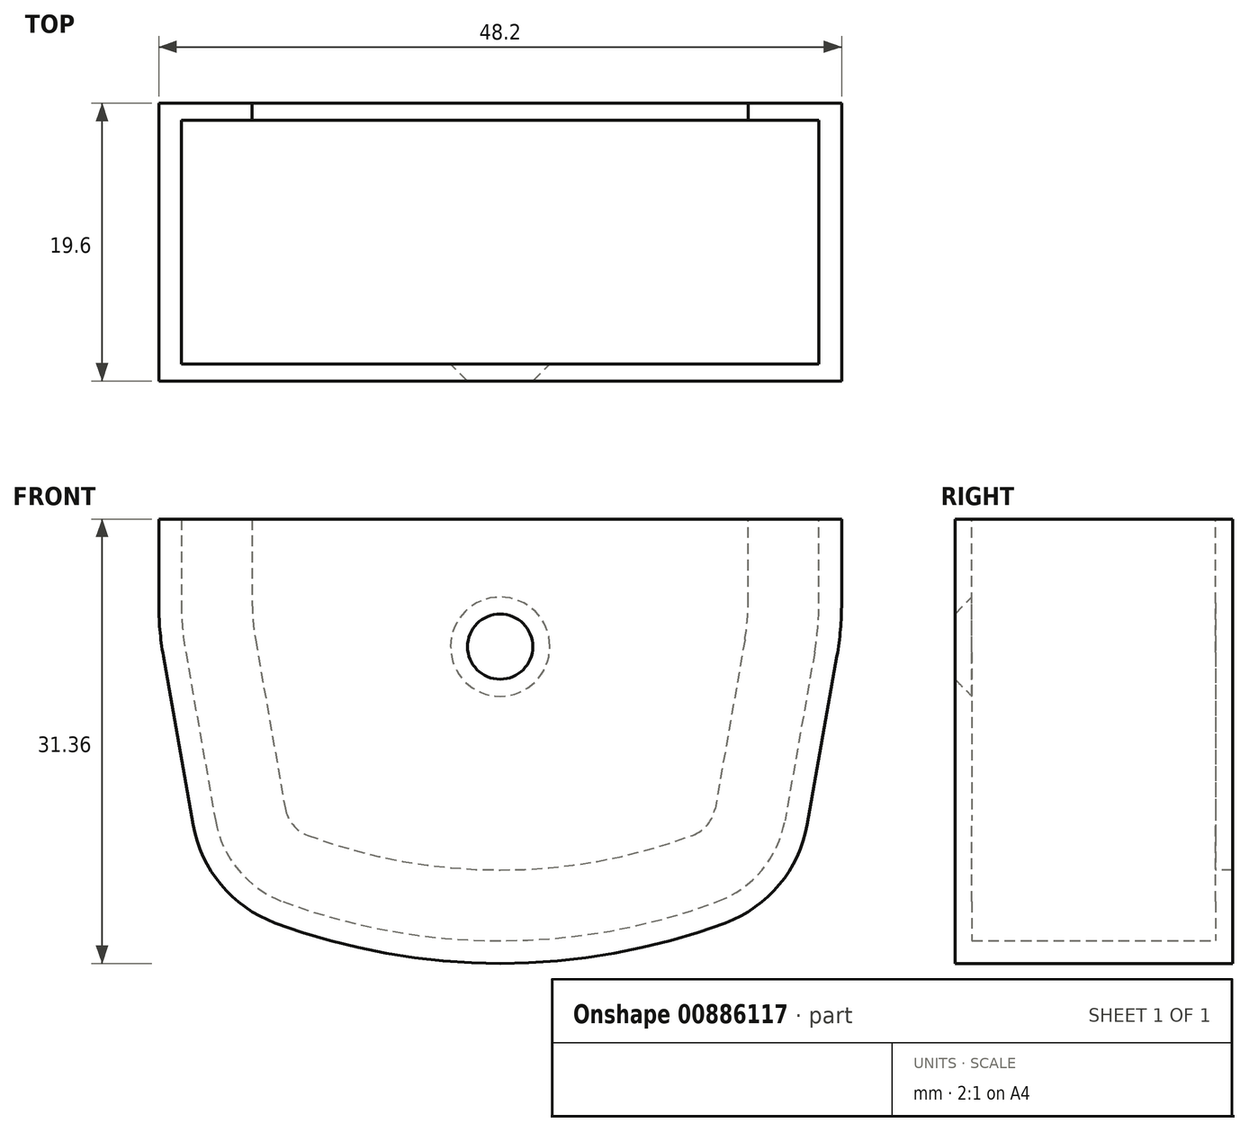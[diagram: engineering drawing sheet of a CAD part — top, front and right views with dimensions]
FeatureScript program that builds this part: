
annotation { "Feature Type Name" : "Feature", "Feature Type Description" : "" }
export const myFeature = defineFeature(function(context is Context, id is Id, definition is map)
    precondition{}
    {
        {
            var Q0;
            Q0=qCreatedBy(makeId("Front.planeOp"),FACE);
            var sketch = newSketch(context, id + "F0", { "sketchPlane" : qUnion([Q0])});
            skLineSegment(sketch, "E0", {"start": v(-22.2, 17.61) * mm, "end": v(-20.1, 5.73) * mm});
            skArc(sketch, "E1.filletArc", {"start": v(-20.1, 5.73) * mm, "mid": v(-18.48, 2.23) * mm, "end": v(-15.33, 0) * mm});
            skArc(sketch, "E2.MirrorCS", {"start": v(20.1, 5.73) * mm, "mid": v(18.48, 2.23) * mm, "end": v(15.33, 0) * mm});
            skLineSegment(sketch, "E3.MirrorCS", {"start": v(22.2, 17.61) * mm, "end": v(20.1, 5.73) * mm});
            skArc(sketch, "E4", {"start": v(-15.33, 0) * mm, "mid": v(0, -2.76) * mm, "end": v(15.33, 0) * mm});
            skLineSegment(sketch, "E5", {"start": v(-22.5, 27) * mm, "end": v(-22.5, 21.09) * mm});
            skLineSegment(sketch, "E6", {"start": v(22.5, 21.09) * mm, "end": v(22.5, 27) * mm});
            skPoint(sketch, "E7.visualSharp", {"position": v(-22.5, 19.34) * mm});
            skArc(sketch, "E7.filletArc", {"start": v(-22.5, 21.09) * mm, "mid": v(-22.42, 19.34) * mm, "end": v(-22.2, 17.61) * mm});
            skPoint(sketch, "E8.visualSharp", {"position": v(22.5, 19.34) * mm});
            skArc(sketch, "E8.filletArc", {"start": v(22.2, 17.61) * mm, "mid": v(22.42, 19.34) * mm, "end": v(22.5, 21.09) * mm});
            skLineSegment(sketch, "E9.0", {"start": v(24.1, 21.09) * mm, "end": v(24.1, 27) * mm});
            skArc(sketch, "E9.1", {"start": v(23.77, 17.34) * mm, "mid": v(24.02, 19.2) * mm, "end": v(24.1, 21.09) * mm});
            skLineSegment(sketch, "E9.2", {"start": v(23.77, 17.34) * mm, "end": v(21.68, 5.45) * mm});
            skArc(sketch, "E9.3", {"start": v(21.68, 5.45) * mm, "mid": v(19.7, 1.2) * mm, "end": v(15.89, -1.5) * mm});
            skArc(sketch, "E9.4", {"start": v(-15.89, -1.5) * mm, "mid": v(0, -4.36) * mm, "end": v(15.89, -1.5) * mm});
            skLineSegment(sketch, "E9.5", {"start": v(-24.1, 27) * mm, "end": v(-24.1, 21.09) * mm});
            skArc(sketch, "E9.6", {"start": v(-24.1, 21.09) * mm, "mid": v(-24.02, 19.2) * mm, "end": v(-23.77, 17.34) * mm});
            skLineSegment(sketch, "E9.7", {"start": v(-23.77, 17.34) * mm, "end": v(-21.68, 5.45) * mm});
            skArc(sketch, "E9.8", {"start": v(-21.68, 5.45) * mm, "mid": v(-19.7, 1.2) * mm, "end": v(-15.89, -1.5) * mm});
            skLineSegment(sketch, "E10", {"start": v(-24.1, 27) * mm, "end": v(-22.5, 27) * mm});
            skLineSegment(sketch, "E11", {"start": v(22.5, 27) * mm, "end": v(24.1, 27) * mm});
            skSolve(sketch);
        }
        {
            var Q0;
            Q0 = qSketchRegion(id + "F0", true);
            extrude(context, id + "F1", {"entities" : qUnion([Q0]), "depth" : 17.2 * mm, "offsetDistance" : 25 * mm});
        }
        {
            var Q0;
            Q0=makeQuery(id+"F1.opExtrude","CAP_FACE",FACE,{"disambiguationData":[OSD([sQuery(id+"F0.wireOp",EDGE,"E0"),sQuery(id+"F0.wireOp",EDGE,"E1.filletArc"),sQuery(id+"F0.wireOp",EDGE,"E2.MirrorCS"),sQuery(id+"F0.wireOp",EDGE,"E3.MirrorCS"),sQuery(id+"F0.wireOp",EDGE,"E4"),sQuery(id+"F0.wireOp",EDGE,"E5"),sQuery(id+"F0.wireOp",EDGE,"E6"),sQuery(id+"F0.wireOp",EDGE,"E7.filletArc"),sQuery(id+"F0.wireOp",EDGE,"E8.filletArc"),sQuery(id+"F0.wireOp",EDGE,"E9.0"),sQuery(id+"F0.wireOp",EDGE,"E9.1"),sQuery(id+"F0.wireOp",EDGE,"E9.2"),sQuery(id+"F0.wireOp",EDGE,"E9.3"),sQuery(id+"F0.wireOp",EDGE,"E9.4"),sQuery(id+"F0.wireOp",EDGE,"E9.5"),sQuery(id+"F0.wireOp",EDGE,"E9.6"),sQuery(id+"F0.wireOp",EDGE,"E9.7"),sQuery(id+"F0.wireOp",EDGE,"E9.8"),sQuery(id+"F0.wireOp",EDGE,"E10"),sQuery(id+"F0.wireOp",EDGE,"E11")])],"isStart":false});
            var sketch = newSketch(context, id + "F2", { "sketchPlane" : qUnion([Q0])});
            skLineSegment(sketch, "E12.0", {"start": v(-24.1, 27) * mm, "end": v(-24.1, 21.09) * mm});
            skArc(sketch, "E13.0", {"start": v(-24.1, 21.09) * mm, "mid": v(-24.02, 19.2) * mm, "end": v(-23.77, 17.34) * mm});
            skLineSegment(sketch, "E14.0", {"start": v(-23.77, 17.34) * mm, "end": v(-21.68, 5.45) * mm});
            skArc(sketch, "E15.0", {"start": v(-21.68, 5.45) * mm, "mid": v(-19.7, 1.2) * mm, "end": v(-15.89, -1.5) * mm});
            skArc(sketch, "E16.0", {"start": v(-15.89, -1.5) * mm, "mid": v(0, -4.36) * mm, "end": v(15.89, -1.5) * mm});
            skArc(sketch, "E17.0", {"start": v(21.68, 5.45) * mm, "mid": v(19.7, 1.2) * mm, "end": v(15.89, -1.5) * mm});
            skLineSegment(sketch, "E18.0", {"start": v(23.77, 17.34) * mm, "end": v(21.68, 5.45) * mm});
            skArc(sketch, "E19.0", {"start": v(23.77, 17.34) * mm, "mid": v(24.02, 19.2) * mm, "end": v(24.1, 21.09) * mm});
            skLineSegment(sketch, "E20.0", {"start": v(24.1, 21.09) * mm, "end": v(24.1, 27) * mm});
            skLineSegment(sketch, "E21", {"start": v(-24.1, 27) * mm, "end": v(24.1, 27) * mm});
            skCircle(sketch, "E22", {"center": v(0, 18) * mm, "radius": 1.5 * mm});
            skSolve(sketch);
        }
        {
            var Q0;
            Q0 = qSketchRegion(id + "F2", true);
            extrude(context, id + "F3", {"entities" : qUnion([Q0]), "operationType" : NewBodyOperationType.ADD, "depth" : 1.2 * mm, "offsetDistance" : 25 * mm});
        }
        {
            var Q0;
            Q0=makeQuery(id+"F1.opExtrude","CAP_FACE",FACE,{"disambiguationData":[OSD([sQuery(id+"F0.wireOp",EDGE,"E0"),sQuery(id+"F0.wireOp",EDGE,"E1.filletArc"),sQuery(id+"F0.wireOp",EDGE,"E2.MirrorCS"),sQuery(id+"F0.wireOp",EDGE,"E3.MirrorCS"),sQuery(id+"F0.wireOp",EDGE,"E4"),sQuery(id+"F0.wireOp",EDGE,"E5"),sQuery(id+"F0.wireOp",EDGE,"E6"),sQuery(id+"F0.wireOp",EDGE,"E7.filletArc"),sQuery(id+"F0.wireOp",EDGE,"E8.filletArc"),sQuery(id+"F0.wireOp",EDGE,"E9.0"),sQuery(id+"F0.wireOp",EDGE,"E9.1"),sQuery(id+"F0.wireOp",EDGE,"E9.2"),sQuery(id+"F0.wireOp",EDGE,"E9.3"),sQuery(id+"F0.wireOp",EDGE,"E9.4"),sQuery(id+"F0.wireOp",EDGE,"E9.5"),sQuery(id+"F0.wireOp",EDGE,"E9.6"),sQuery(id+"F0.wireOp",EDGE,"E9.7"),sQuery(id+"F0.wireOp",EDGE,"E9.8"),sQuery(id+"F0.wireOp",EDGE,"E10"),sQuery(id+"F0.wireOp",EDGE,"E11")])],"isStart":true});
            var sketch = newSketch(context, id + "F4", { "sketchPlane" : qUnion([Q0])});
            skLineSegment(sketch, "E23.0", {"start": v(-24.1, 21.09) * mm, "end": v(-24.1, 27) * mm});
            skArc(sketch, "E24.0", {"start": v(-23.77, 17.34) * mm, "mid": v(-24.02, 19.2) * mm, "end": v(-24.1, 21.09) * mm});
            skLineSegment(sketch, "E25.0", {"start": v(-23.77, 17.34) * mm, "end": v(-21.68, 5.45) * mm});
            skArc(sketch, "E26.0", {"start": v(-21.68, 5.45) * mm, "mid": v(-19.7, 1.2) * mm, "end": v(-15.89, -1.5) * mm});
            skArc(sketch, "E27.0", {"start": v(15.89, -1.5) * mm, "mid": v(0, -4.36) * mm, "end": v(-15.89, -1.5) * mm});
            skArc(sketch, "E28.0", {"start": v(21.68, 5.45) * mm, "mid": v(19.7, 1.2) * mm, "end": v(15.89, -1.5) * mm});
            skLineSegment(sketch, "E29.0", {"start": v(23.77, 17.34) * mm, "end": v(21.68, 5.45) * mm});
            skArc(sketch, "E30.0", {"start": v(24.1, 21.09) * mm, "mid": v(24.02, 19.2) * mm, "end": v(23.77, 17.34) * mm});
            skLineSegment(sketch, "E31.0", {"start": v(24.1, 27) * mm, "end": v(24.1, 21.09) * mm});
            skLineSegment(sketch, "E32.0", {"start": v(-17.5, 27) * mm, "end": v(-24.1, 27) * mm});
            skLineSegment(sketch, "E33.0", {"start": v(24.1, 27) * mm, "end": v(17.5, 27) * mm});
            skLineSegment(sketch, "E34.0", {"start": v(-17.5, 21.09) * mm, "end": v(-17.5, 27) * mm});
            skArc(sketch, "E34.1", {"start": v(-17.27, 18.48) * mm, "mid": v(-17.44, 19.78) * mm, "end": v(-17.5, 21.09) * mm});
            skLineSegment(sketch, "E34.2", {"start": v(-17.27, 18.48) * mm, "end": v(-15.18, 6.6) * mm});
            skArc(sketch, "E34.3", {"start": v(-15.18, 6.6) * mm, "mid": v(-14.64, 5.43) * mm, "end": v(-13.59, 4.69) * mm});
            skArc(sketch, "E34.4", {"start": v(13.59, 4.69) * mm, "mid": v(0, 2.24) * mm, "end": v(-13.59, 4.69) * mm});
            skLineSegment(sketch, "E34.5", {"start": v(17.5, 27) * mm, "end": v(17.5, 21.09) * mm});
            skArc(sketch, "E34.6", {"start": v(17.5, 21.09) * mm, "mid": v(17.44, 19.78) * mm, "end": v(17.27, 18.48) * mm});
            skLineSegment(sketch, "E34.7", {"start": v(17.27, 18.48) * mm, "end": v(15.18, 6.6) * mm});
            skArc(sketch, "E34.8", {"start": v(15.18, 6.6) * mm, "mid": v(14.64, 5.43) * mm, "end": v(13.59, 4.69) * mm});
            skSolve(sketch);
        }
        {
            var Q0;
            Q0 = qSketchRegion(id + "F4", true);
            extrude(context, id + "F5", {"entities" : qUnion([Q0]), "operationType" : NewBodyOperationType.ADD, "depth" : 1.2 * mm, "offsetDistance" : 25 * mm});
        }
        {
            var Q0;
            Q0=makeQuery(id+"F3.opExtrude","CAP_EDGE",EDGE,{"disambiguationData":[OSD([sQuery(id+"F2.wireOp",EDGE,"E22")])],"isStart":true});
            chamfer(context, id + "F6", {"entities" : qUnion([Q0]), "width" : 2 * mm, "tangentPropagation" : true});
        }
    });
